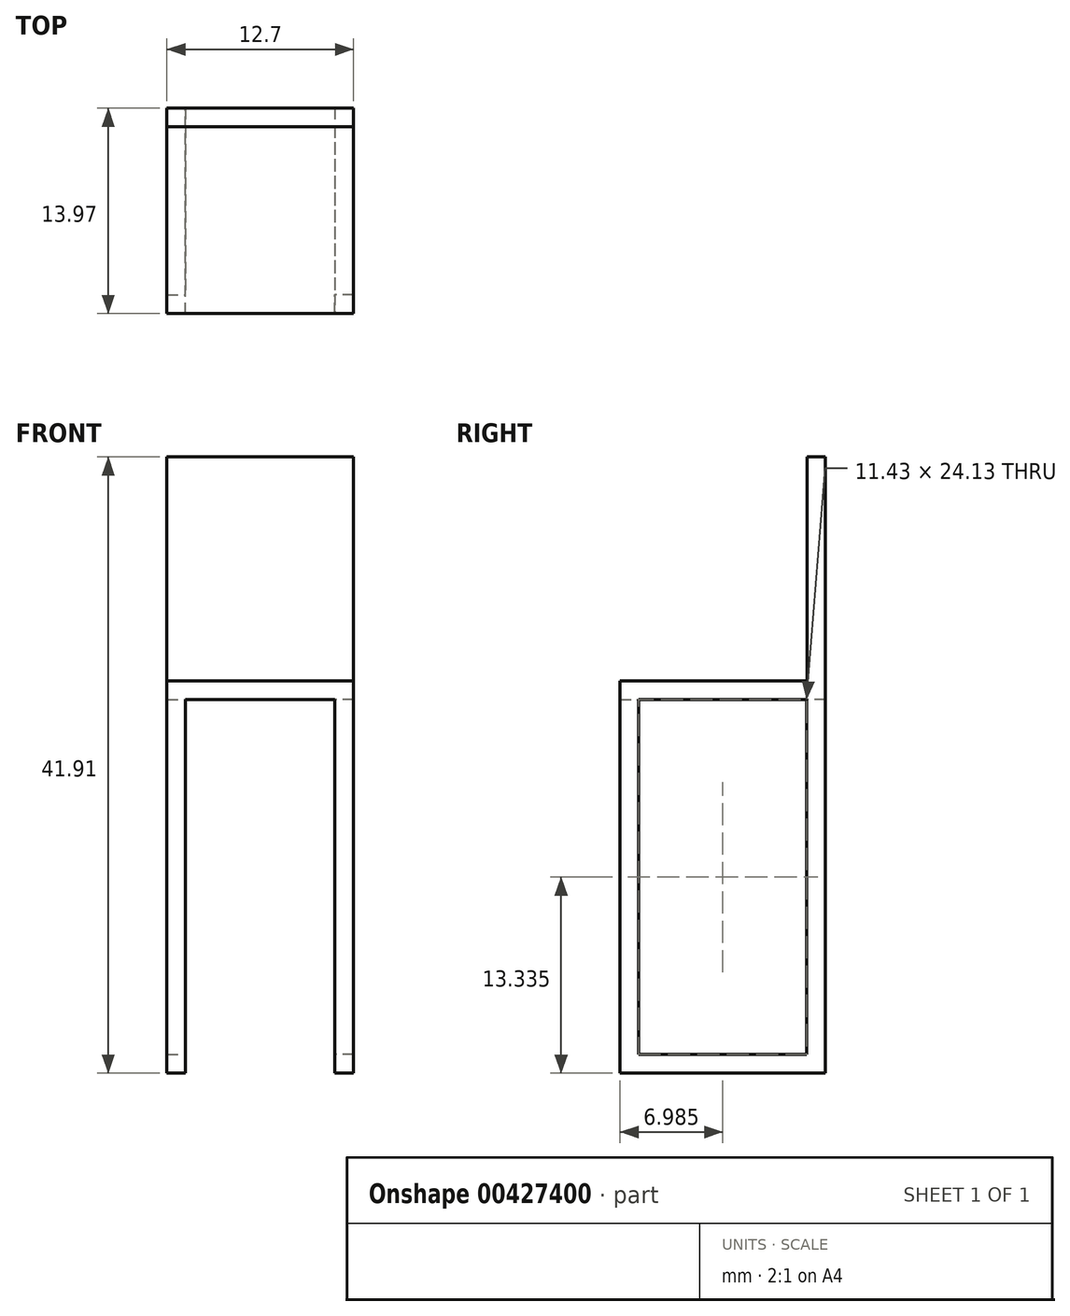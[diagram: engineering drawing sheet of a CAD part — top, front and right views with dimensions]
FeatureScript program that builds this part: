
annotation { "Feature Type Name" : "Feature", "Feature Type Description" : "" }
export const myFeature = defineFeature(function(context is Context, id is Id, definition is map)
    precondition{}
    {
        {
            var Q0;
            Q0=qCreatedBy(makeId("Front.planeOp"),FACE);
            var sketch = newSketch(context, id + "F0", { "sketchPlane" : qUnion([Q0])});
            skLineSegment(sketch, "E0", {"start": v(0, 0) * mm, "end": v(-6.35, 0) * mm});
            skLineSegment(sketch, "E1", {"start": v(-6.35, 0) * mm, "end": v(-6.35, 1.27) * mm});
            skLineSegment(sketch, "E2", {"start": v(-6.35, 1.27) * mm, "end": v(0, 1.27) * mm});
            skLineSegment(sketch, "E3.MirrorCS", {"start": v(0, 0) * mm, "end": v(6.35, 0) * mm});
            skLineSegment(sketch, "E4.MirrorCS", {"start": v(6.35, 1.27) * mm, "end": v(0, 1.27) * mm});
            skLineSegment(sketch, "E5.MirrorCS", {"start": v(6.35, 0) * mm, "end": v(6.35, 1.27) * mm});
            skSolve(sketch);
        }
        {
            var Q0;
            Q0 = qSketchRegion(id + "F0", true);
            extrude(context, id + "F1", {"entities" : qUnion([Q0]), "depth" : 13.97 * mm});
        }
        {
            var Q0;
            Q0=makeQuery(id+"F1.opExtrude","SWEPT_FACE",FACE,{"disambiguationData":[OSD([sQuery(id+"F0.wireOp",EDGE,"E2"),sQuery(id+"F0.wireOp",EDGE,"E4.MirrorCS")])]});
            var sketch = newSketch(context, id + "F2", { "sketchPlane" : qUnion([Q0])});
            skLineSegment(sketch, "E6", {"start": v(6.35, 0) * mm, "end": v(6.35, -1.26) * mm});
            skLineSegment(sketch, "E7", {"start": v(6.35, -1.26) * mm, "end": v(-6.35, -1.26) * mm});
            skLineSegment(sketch, "E8", {"start": v(-6.35, -1.26) * mm, "end": v(-6.35, 0) * mm});
            skLineSegment(sketch, "E9", {"start": v(-6.35, 0) * mm, "end": v(6.35, 0) * mm});
            skSolve(sketch);
        }
        {
            var Q0;
            Q0 = qSketchRegion(id + "F2", true);
            extrude(context, id + "F3", {"entities" : qUnion([Q0]), "operationType" : NewBodyOperationType.ADD, "depth" : 15.24 * mm});
        }
        {
            var Q0;
            Q0=makeQuery(id+"F1.opExtrude","SWEPT_FACE",FACE,{"disambiguationData":[OSD([sQuery(id+"F0.wireOp",EDGE,"E0"),sQuery(id+"F0.wireOp",EDGE,"E3.MirrorCS")])]});
            var sketch = newSketch(context, id + "F4", { "sketchPlane" : qUnion([Q0])});
            skLineSegment(sketch, "E10.bottom", {"start": v(-6.35, 13.97) * mm, "end": v(-5.08, 13.97) * mm});
            skLineSegment(sketch, "E10.top", {"start": v(-6.35, 12.7) * mm, "end": v(-5.08, 12.7) * mm});
            skLineSegment(sketch, "E10.left", {"start": v(-6.35, 13.97) * mm, "end": v(-6.35, 12.7) * mm});
            skLineSegment(sketch, "E10.right", {"start": v(-5.08, 13.97) * mm, "end": v(-5.08, 12.7) * mm});
            skLineSegment(sketch, "E11.bottom", {"start": v(-6.35, 0) * mm, "end": v(-5.08, 0) * mm});
            skLineSegment(sketch, "E11.top", {"start": v(-6.35, 1.27) * mm, "end": v(-5.08, 1.27) * mm});
            skLineSegment(sketch, "E11.left", {"start": v(-6.35, 0) * mm, "end": v(-6.35, 1.27) * mm});
            skLineSegment(sketch, "E11.right", {"start": v(-5.08, 0) * mm, "end": v(-5.08, 1.27) * mm});
            skLineSegment(sketch, "E12.MirrorCS", {"start": v(6.35, 1.27) * mm, "end": v(5.08, 1.27) * mm});
            skLineSegment(sketch, "E13.MirrorCS", {"start": v(6.35, 0) * mm, "end": v(6.35, 1.27) * mm});
            skLineSegment(sketch, "E14.MirrorCS", {"start": v(5.08, 0) * mm, "end": v(5.08, 1.27) * mm});
            skLineSegment(sketch, "E15.MirrorCS", {"start": v(6.35, 0) * mm, "end": v(5.08, 0) * mm});
            skLineSegment(sketch, "E16.MirrorCS", {"start": v(6.35, 13.97) * mm, "end": v(5.08, 13.97) * mm});
            skLineSegment(sketch, "E17.MirrorCS", {"start": v(5.08, 13.97) * mm, "end": v(5.08, 12.7) * mm});
            skLineSegment(sketch, "E18.MirrorCS", {"start": v(6.35, 12.7) * mm, "end": v(5.08, 12.7) * mm});
            skLineSegment(sketch, "E19.MirrorCS", {"start": v(6.35, 13.97) * mm, "end": v(6.35, 12.7) * mm});
            skSolve(sketch);
        }
        {
            var Q0;
            Q0 = qSketchRegion(id + "F4", true);
            extrude(context, id + "F5", {"entities" : qUnion([Q0]), "operationType" : NewBodyOperationType.ADD, "depth" : 25.4 * mm});
        }
        {
            var Q0;
            Q0=makeQuery(id+"F5.opExtrude","SWEPT_FACE",FACE,{"disambiguationData":[OSD([sQuery(id+"F4.wireOp",EDGE,"E18.MirrorCS")])]});
            var sketch = newSketch(context, id + "F6", { "sketchPlane" : qUnion([Q0])});
            skLineSegment(sketch, "E20.bottom", {"start": v(-5.08, -25.4) * mm, "end": v(-6.35, -25.4) * mm});
            skLineSegment(sketch, "E20.top", {"start": v(-5.08, -24.13) * mm, "end": v(-6.35, -24.13) * mm});
            skLineSegment(sketch, "E20.left", {"start": v(-5.08, -25.4) * mm, "end": v(-5.08, -24.13) * mm});
            skLineSegment(sketch, "E20.right", {"start": v(-6.35, -25.4) * mm, "end": v(-6.35, -24.13) * mm});
            skSolve(sketch);
        }
        {
            var Q0;
            Q0 = qSketchRegion(id + "F6", true);
            extrude(context, id + "F7", {"entities" : qUnion([Q0]), "operationType" : NewBodyOperationType.ADD, "depth" : 12.7 * mm});
        }
        {
            var Q0;
            Q0=makeQuery(id+"F1.opExtrude","SWEPT_BODY",BODY,{"disambiguationData":[OSD([sQuery(id+"F0.wireOp",EDGE,"E0"),sQuery(id+"F0.wireOp",EDGE,"E1"),sQuery(id+"F0.wireOp",EDGE,"E2"),sQuery(id+"F0.wireOp",EDGE,"E3.MirrorCS"),sQuery(id+"F0.wireOp",EDGE,"E4.MirrorCS"),sQuery(id+"F0.wireOp",EDGE,"E5.MirrorCS")])]});
            var Q1;
            Q1=qCreatedBy(makeId("Right.planeOp"),FACE);
            mirror(context, id + "F8", {"operationType" : NewBodyOperationType.ADD, "entities" : qUnion([Q0]), "mirrorPlane" : qUnion([Q1])});
        }
    });
